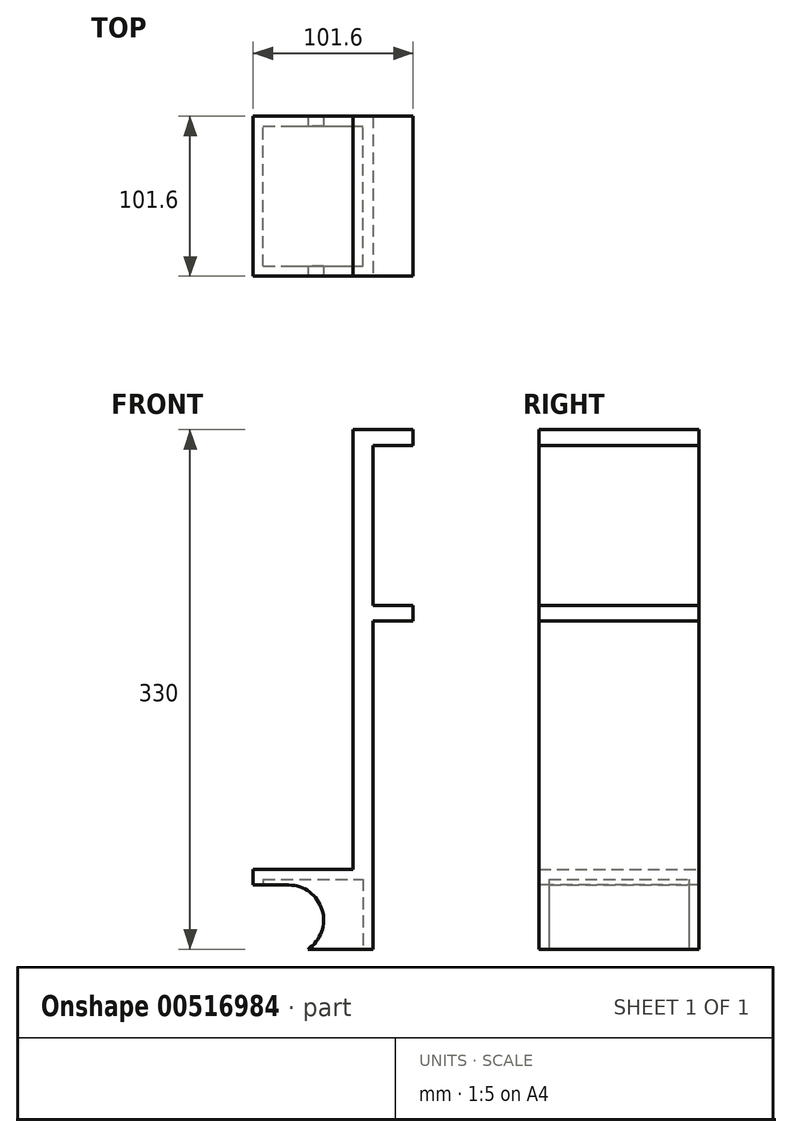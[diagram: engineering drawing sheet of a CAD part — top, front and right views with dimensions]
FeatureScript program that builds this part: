
annotation { "Feature Type Name" : "Feature", "Feature Type Description" : "" }
export const myFeature = defineFeature(function(context is Context, id is Id, definition is map)
    precondition{}
    {
        {
            var Q0;
            Q0=qCreatedBy(makeId("Top.planeOp"),FACE);
            var sketch = newSketch(context, id + "F0", { "sketchPlane" : qUnion([Q0])});
            skLineSegment(sketch, "E0.bottom", {"start": v(-38.1, 50.8) * mm, "end": v(38.1, 50.8) * mm});
            skLineSegment(sketch, "E0.top", {"start": v(-38.1, -50.8) * mm, "end": v(38.1, -50.8) * mm});
            skLineSegment(sketch, "E0.left", {"start": v(-38.1, 50.8) * mm, "end": v(-38.1, -50.8) * mm});
            skLineSegment(sketch, "E0.right", {"start": v(38.1, 50.8) * mm, "end": v(38.1, -50.8) * mm});
            skPoint(sketch, "E0.middle", {"position": v(0, 0) * mm});
            skSolve(sketch);
        }
        {
            var Q0;
            Q0 = qSketchRegion(id + "F0", true);
            extrude(context, id + "F1", {"entities" : qUnion([Q0]), "depth" : 50.8 * mm, "offsetDistance" : 25.4 * mm});
        }
        {
            var Q0;
            Q0=makeQuery(id+"F1.opExtrude","SWEPT_FACE",FACE,{"disambiguationData":[OSD([sQuery(id+"F0.wireOp",EDGE,"E0.right")])]});
            var sketch = newSketch(context, id + "F2", { "sketchPlane" : qUnion([Q0])});
            skLineSegment(sketch, "E1.bottom", {"start": v(-50.8, 0) * mm, "end": v(50.8, 0) * mm});
            skLineSegment(sketch, "E1.top", {"start": v(-50.8, 330) * mm, "end": v(50.8, 330) * mm});
            skLineSegment(sketch, "E1.left", {"start": v(-50.8, 0) * mm, "end": v(-50.8, 330) * mm});
            skLineSegment(sketch, "E1.right", {"start": v(50.8, 0) * mm, "end": v(50.8, 330) * mm});
            skSolve(sketch);
        }
        {
            var Q0;
            Q0 = qSketchRegion(id + "F2", true);
            extrude(context, id + "F3", {"entities" : qUnion([Q0]), "operationType" : NewBodyOperationType.ADD, "oppositeDirection" : true, "depth" : 12.7 * mm, "offsetDistance" : 25.4 * mm});
        }
        {
            var Q0;
            Q0=makeQuery(id+"F3.boolean.opBoolean","MERGE",FACE,{"derivedFrom":[makeQuery(id+"F1.opExtrude","SWEPT_FACE",FACE,{"disambiguationData":[OSD([sQuery(id+"F0.wireOp",EDGE,"E0.right")])]}),makeQuery(id+"F3.opExtrude","CAP_FACE",FACE,{"disambiguationData":[OSD([sQuery(id+"F2.wireOp",EDGE,"E1.bottom"),sQuery(id+"F2.wireOp",EDGE,"E1.top"),sQuery(id+"F2.wireOp",EDGE,"E1.left"),sQuery(id+"F2.wireOp",EDGE,"E1.right")])],"isStart":true})]});
            var sketch = newSketch(context, id + "F4", { "sketchPlane" : qUnion([Q0])});
            skLineSegment(sketch, "E2.bottom", {"start": v(-50.8, 330) * mm, "end": v(50.8, 330) * mm});
            skLineSegment(sketch, "E2.top", {"start": v(-50.8, 320) * mm, "end": v(50.8, 320) * mm});
            skLineSegment(sketch, "E2.left", {"start": v(-50.8, 330) * mm, "end": v(-50.8, 320) * mm});
            skLineSegment(sketch, "E2.right", {"start": v(50.8, 330) * mm, "end": v(50.8, 320) * mm});
            skLineSegment(sketch, "E3.bottom", {"start": v(-50.8, 218.4) * mm, "end": v(50.8, 218.4) * mm});
            skLineSegment(sketch, "E3.top", {"start": v(-50.8, 208.4) * mm, "end": v(50.8, 208.4) * mm});
            skLineSegment(sketch, "E3.left", {"start": v(-50.8, 218.4) * mm, "end": v(-50.8, 208.4) * mm});
            skLineSegment(sketch, "E3.right", {"start": v(50.8, 218.4) * mm, "end": v(50.8, 208.4) * mm});
            skSolve(sketch);
        }
        {
            var Q0;
            Q0 = qSketchRegion(id + "F4", true);
            extrude(context, id + "F5", {"entities" : qUnion([Q0]), "operationType" : NewBodyOperationType.ADD, "depth" : 25.4 * mm, "offsetDistance" : 25.4 * mm});
        }
        {
            var Q0;
            Q0=makeQuery(id+"F1.opExtrude","CAP_FACE",FACE,{"disambiguationData":[OSD([sQuery(id+"F0.wireOp",EDGE,"E0.bottom"),sQuery(id+"F0.wireOp",EDGE,"E0.top"),sQuery(id+"F0.wireOp",EDGE,"E0.left"),sQuery(id+"F0.wireOp",EDGE,"E0.right")])],"isStart":true});
            var sketch = newSketch(context, id + "F6", { "sketchPlane" : qUnion([Q0])});
            skLineSegment(sketch, "E4.bottom", {"start": v(-31.75, 44.45) * mm, "end": v(31.75, 44.45) * mm});
            skLineSegment(sketch, "E4.top", {"start": v(-31.75, -44.45) * mm, "end": v(31.75, -44.45) * mm});
            skLineSegment(sketch, "E4.left", {"start": v(-31.75, 44.45) * mm, "end": v(-31.75, -44.45) * mm});
            skLineSegment(sketch, "E4.right", {"start": v(31.75, 44.45) * mm, "end": v(31.75, -44.45) * mm});
            skPoint(sketch, "E4.middle", {"position": v(0, 0) * mm});
            skSolve(sketch);
        }
        {
            var Q0;
            Q0=makeQuery(id+"F6.imprint","IMPRINT",FACE,{"disambiguationData":[TD([[makeQuery(id+"F6.imprint","IMPRINT",EDGE,{"derivedFrom":sQuery(id+"F6.wireOp",EDGE,"E4.bottom")}),-1.0]])]});
            extrude(context, id + "F7", {"entities" : qUnion([Q0]), "operationType" : NewBodyOperationType.REMOVE, "oppositeDirection" : true, "depth" : 44.45 * mm, "offsetDistance" : 25.4 * mm});
        }
        {
            var Q0;
            Q0=makeQuery(id+"F5.boolean.opBoolean","MERGE",FACE,{"derivedFrom":[makeQuery(id+"F3.boolean.opBoolean","MERGE",FACE,{"derivedFrom":[makeQuery(id+"F1.opExtrude","SWEPT_FACE",FACE,{"disambiguationData":[OSD([sQuery(id+"F0.wireOp",EDGE,"E0.top")])]}),makeQuery(id+"F3.opExtrude","SWEPT_FACE",FACE,{"disambiguationData":[OSD([sQuery(id+"F2.wireOp",EDGE,"E1.left")])]})]}),makeQuery(id+"F5.opExtrude","SWEPT_FACE",FACE,{"disambiguationData":[OSD([sQuery(id+"F4.wireOp",EDGE,"E2.left")])]}),makeQuery(id+"F5.opExtrude","SWEPT_FACE",FACE,{"disambiguationData":[OSD([sQuery(id+"F4.wireOp",EDGE,"E3.left")])]})]});
            var sketch = newSketch(context, id + "F8", { "sketchPlane" : qUnion([Q0])});
            skCircle(sketch, "E5", {"center": v(-15.55, 18.56) * mm, "radius": 22.23 * mm});
            skLineSegment(sketch, "E6", {"start": v(-15.55, 40.78) * mm, "end": v(-38.1, 40.78) * mm});
            skLineSegment(sketch, "E7", {"start": v(-38.1, 40.78) * mm, "end": v(-38.1, 0) * mm});
            skLineSegment(sketch, "E8", {"start": v(-38.1, 0) * mm, "end": v(-27.78, 0) * mm});
            skSolve(sketch);
        }
        {
            var Q0;
            Q0 = qSketchRegion(id + "F8", true);
            extrude(context, id + "F9", {"entities" : qUnion([Q0]), "operationType" : NewBodyOperationType.REMOVE, "oppositeDirection" : true, "depth" : 114.8 * mm, "offsetDistance" : 25.4 * mm});
        }
    });
